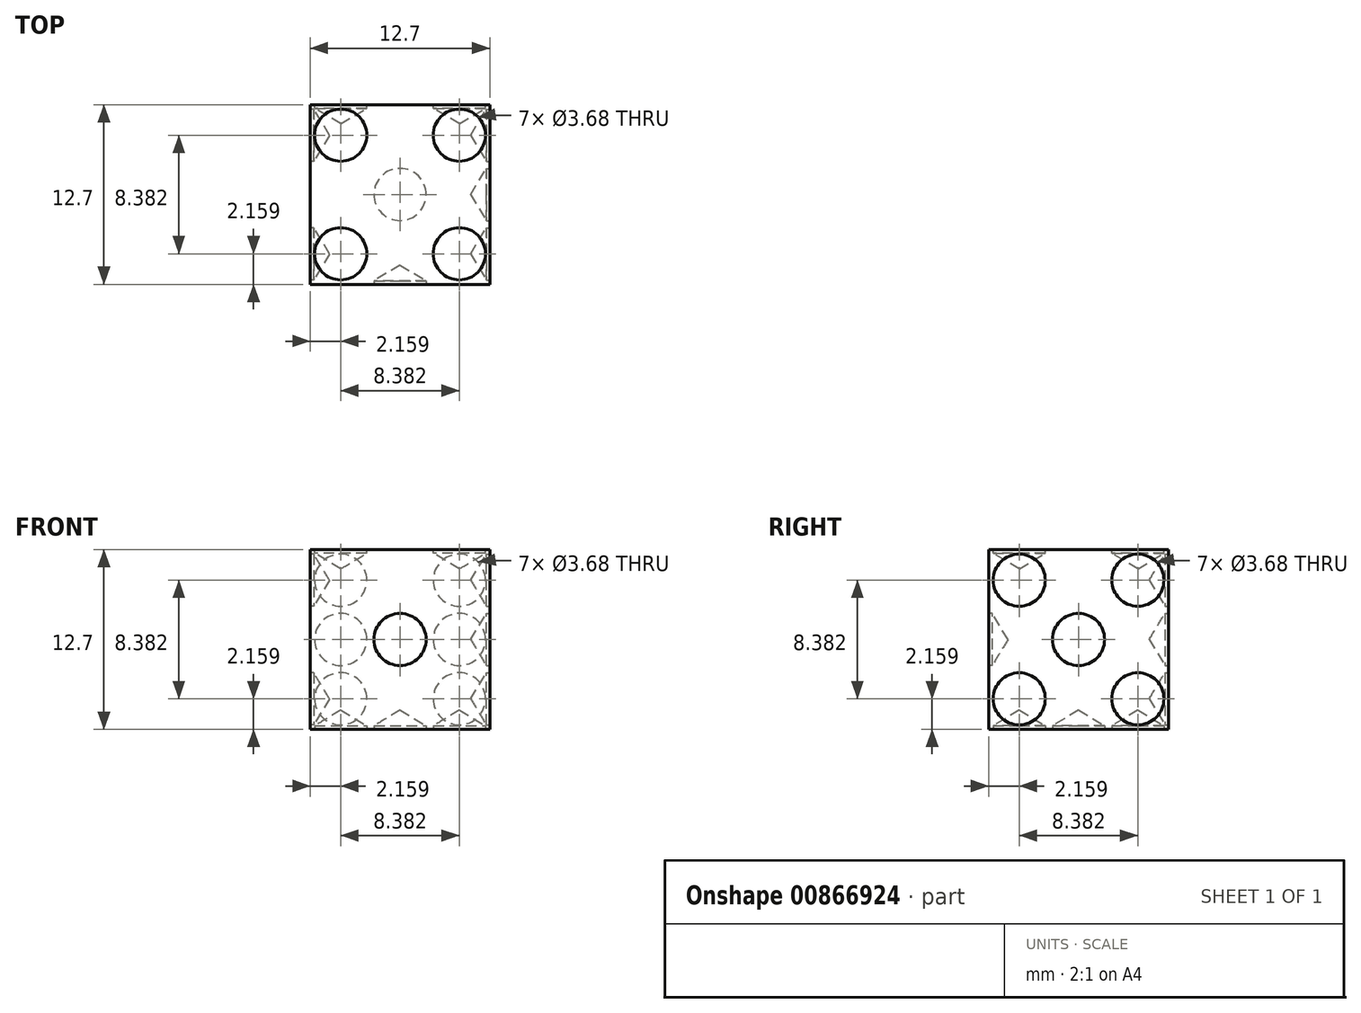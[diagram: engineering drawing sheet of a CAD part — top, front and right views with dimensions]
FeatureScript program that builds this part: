
annotation { "Feature Type Name" : "Feature", "Feature Type Description" : "" }
export const myFeature = defineFeature(function(context is Context, id is Id, definition is map)
    precondition{}
    {
        {
            var Q0;
            Q0=qCreatedBy(makeId("Top.planeOp"),FACE);
            var sketch = newSketch(context, id + "F0", { "sketchPlane" : qUnion([Q0])});
            skLineSegment(sketch, "E0.bottom", {"start": v(6.35, 6.35) * mm, "end": v(-6.35, 6.35) * mm});
            skLineSegment(sketch, "E0.top", {"start": v(6.35, -6.35) * mm, "end": v(-6.35, -6.35) * mm});
            skLineSegment(sketch, "E0.left", {"start": v(6.35, 6.35) * mm, "end": v(6.35, -6.35) * mm});
            skLineSegment(sketch, "E0.right", {"start": v(-6.35, 6.35) * mm, "end": v(-6.35, -6.35) * mm});
            skPoint(sketch, "E0.middle", {"position": v(0, 0) * mm});
            skSolve(sketch);
        }
        {
            var Q0;
            Q0=makeQuery(id+"F0.imprint","IMPRINT",FACE,{"disambiguationData":[TD([[makeQuery(id+"F0.imprint","IMPRINT",EDGE,{"derivedFrom":sQuery(id+"F0.wireOp",EDGE,"E0.bottom")}),1.0]])]});
            extrude(context, id + "F1", {"entities" : qUnion([Q0]), "depth" : 6.35 * mm, "offsetDistance" : 25.4 * mm, "hasSecondDirection" : true, "secondDirectionOppositeDirection" : true, "secondDirectionDepth" : 6.35 * mm});
        }
        {
            var Q0;
            Q0=makeQuery(id+"F1.opExtrude","CAP_FACE",FACE,{"disambiguationData":[OSD([sQuery(id+"F0.wireOp",EDGE,"E0.bottom"),sQuery(id+"F0.wireOp",EDGE,"E0.top"),sQuery(id+"F0.wireOp",EDGE,"E0.left"),sQuery(id+"F0.wireOp",EDGE,"E0.right")])],"isStart":false});
            var sketch = newSketch(context, id + "F2", { "sketchPlane" : qUnion([Q0])});
            skCircle(sketch, "E1", {"center": v(-4.2, 4.2) * mm, "radius": 1.9 * mm});
            skCircle(sketch, "E2", {"center": v(4.2, 4.2) * mm, "radius": 1.9 * mm});
            skCircle(sketch, "E3", {"center": v(-4.2, -4.2) * mm, "radius": 1.9 * mm});
            skCircle(sketch, "E4", {"center": v(4.2, -4.2) * mm, "radius": 1.9 * mm});
            skSolve(sketch);
        }
        {
            var Q0;
            Q0=makeQuery(id+"F1.opExtrude","SWEPT_FACE",FACE,{"disambiguationData":[OSD([sQuery(id+"F0.wireOp",EDGE,"E0.left")])]});
            var sketch = newSketch(context, id + "F3", { "sketchPlane" : qUnion([Q0])});
            skCircle(sketch, "E5", {"center": v(-4.2, 4.2) * mm, "radius": 1.9 * mm});
            skCircle(sketch, "E6", {"center": v(4.2, 4.2) * mm, "radius": 1.9 * mm});
            skCircle(sketch, "E7", {"center": v(0, 0) * mm, "radius": 1.9 * mm});
            skCircle(sketch, "E8", {"center": v(-4.2, -4.2) * mm, "radius": 1.9 * mm});
            skCircle(sketch, "E9", {"center": v(4.2, -4.2) * mm, "radius": 1.9 * mm});
            skSolve(sketch);
        }
        {
            var Q0;
            Q0=makeQuery(id+"F1.opExtrude","SWEPT_FACE",FACE,{"disambiguationData":[OSD([sQuery(id+"F0.wireOp",EDGE,"E0.top")])]});
            var sketch = newSketch(context, id + "F4", { "sketchPlane" : qUnion([Q0])});
            skCircle(sketch, "E10", {"center": v(0, 0) * mm, "radius": 1.9 * mm});
            skSolve(sketch);
        }
        {
            var Q0;
            Q0=makeQuery(id+"F1.opExtrude","CAP_FACE",FACE,{"disambiguationData":[OSD([sQuery(id+"F0.wireOp",EDGE,"E0.bottom"),sQuery(id+"F0.wireOp",EDGE,"E0.top"),sQuery(id+"F0.wireOp",EDGE,"E0.left"),sQuery(id+"F0.wireOp",EDGE,"E0.right")])],"isStart":true});
            var sketch = newSketch(context, id + "F5", { "sketchPlane" : qUnion([Q0])});
            skCircle(sketch, "E11", {"center": v(0, 0) * mm, "radius": 1.9 * mm});
            skCircle(sketch, "E12", {"center": v(-4.2, 4.2) * mm, "radius": 1.9 * mm});
            skCircle(sketch, "E13", {"center": v(4.2, -4.2) * mm, "radius": 1.9 * mm});
            skSolve(sketch);
        }
        {
            var Q0;
            Q0=makeQuery(id+"F1.opExtrude","SWEPT_FACE",FACE,{"disambiguationData":[OSD([sQuery(id+"F0.wireOp",EDGE,"E0.right")])]});
            var sketch = newSketch(context, id + "F6", { "sketchPlane" : qUnion([Q0])});
            skCircle(sketch, "E14", {"center": v(4.2, 4.2) * mm, "radius": 1.9 * mm});
            skCircle(sketch, "E15", {"center": v(-4.2, -4.2) * mm, "radius": 1.9 * mm});
            skSolve(sketch);
        }
        {
            var Q0;
            Q0=makeQuery(id+"F1.opExtrude","SWEPT_FACE",FACE,{"disambiguationData":[OSD([sQuery(id+"F0.wireOp",EDGE,"E0.bottom")])]});
            var sketch = newSketch(context, id + "F7", { "sketchPlane" : qUnion([Q0])});
            skCircle(sketch, "E16", {"center": v(-4.2, 4.2) * mm, "radius": 1.9 * mm});
            skCircle(sketch, "E17", {"center": v(-4.2, 0) * mm, "radius": 1.9 * mm});
            skCircle(sketch, "E18", {"center": v(-4.2, -4.2) * mm, "radius": 1.9 * mm});
            skCircle(sketch, "E19", {"center": v(4.2, -4.2) * mm, "radius": 1.9 * mm});
            skCircle(sketch, "E20", {"center": v(4.2, 0) * mm, "radius": 1.9 * mm});
            skCircle(sketch, "E21", {"center": v(4.2, 4.2) * mm, "radius": 1.9 * mm});
            skSolve(sketch);
        }
        {
            var Q0;
            Q0=sQuery(id+"F7.wireOp",VERTEX,"E16.center");
            var Q1;
            Q1=sQuery(id+"F7.wireOp",VERTEX,"E17.center");
            var Q2;
            Q2=sQuery(id+"F7.wireOp",VERTEX,"E18.center");
            var Q3;
            Q3=sQuery(id+"F7.wireOp",VERTEX,"E21.center");
            var Q4;
            Q4=sQuery(id+"F7.wireOp",VERTEX,"E20.center");
            var Q5;
            Q5=sQuery(id+"F7.wireOp",VERTEX,"E19.center");
            var Q6;
            Q6=makeQuery(id+"F1.opExtrude","SWEPT_BODY",BODY,{"disambiguationData":[OSD([sQuery(id+"F0.wireOp",EDGE,"E0.bottom"),sQuery(id+"F0.wireOp",EDGE,"E0.top"),sQuery(id+"F0.wireOp",EDGE,"E0.left"),sQuery(id+"F0.wireOp",EDGE,"E0.right")])]});
            hole(context, id + "F8", {"style" : HoleStyle.SIMPLE, "endStyle" : HoleEndStyle.BLIND, "holeDiameter" : 3.68 * mm, "majorDiameter" : 6.35 * mm, "holeDepth" : 0.25 * mm, "isTappedThrough" : true, "tappedDepth" : 12.7 * mm, "tapClearance" : 3, "locations" : qUnion([Q0, Q1, Q2, Q3, Q4, Q5]), "scope" : qUnion([Q6])});
        }
        {
            var Q0;
            Q0=sQuery(id+"F3.wireOp",VERTEX,"E5.center");
            var Q1;
            Q1=sQuery(id+"F3.wireOp",VERTEX,"E8.center");
            var Q2;
            Q2=sQuery(id+"F3.wireOp",VERTEX,"E6.center");
            var Q3;
            Q3=sQuery(id+"F3.wireOp",VERTEX,"E9.center");
            var Q4;
            Q4=sQuery(id+"F3.wireOp",VERTEX,"E7.center");
            var Q5;
            Q5=makeQuery(id+"F1.opExtrude","SWEPT_BODY",BODY,{"disambiguationData":[OSD([sQuery(id+"F0.wireOp",EDGE,"E0.bottom"),sQuery(id+"F0.wireOp",EDGE,"E0.top"),sQuery(id+"F0.wireOp",EDGE,"E0.left"),sQuery(id+"F0.wireOp",EDGE,"E0.right")])]});
            hole(context, id + "F9", {"style" : HoleStyle.SIMPLE, "endStyle" : HoleEndStyle.BLIND, "holeDiameter" : 3.68 * mm, "majorDiameter" : 6.35 * mm, "holeDepth" : 0.25 * mm, "isTappedThrough" : true, "tappedDepth" : 12.7 * mm, "tapClearance" : 3, "locations" : qUnion([Q0, Q1, Q2, Q3, Q4]), "scope" : qUnion([Q5])});
        }
        {
            var Q0;
            Q0=sQuery(id+"F6.wireOp",VERTEX,"E14.center");
            var Q1;
            Q1=sQuery(id+"F6.wireOp",VERTEX,"E15.center");
            var Q2;
            Q2=makeQuery(id+"F1.opExtrude","SWEPT_BODY",BODY,{"disambiguationData":[OSD([sQuery(id+"F0.wireOp",EDGE,"E0.bottom"),sQuery(id+"F0.wireOp",EDGE,"E0.top"),sQuery(id+"F0.wireOp",EDGE,"E0.left"),sQuery(id+"F0.wireOp",EDGE,"E0.right")])]});
            hole(context, id + "F10", {"style" : HoleStyle.SIMPLE, "endStyle" : HoleEndStyle.BLIND, "holeDiameter" : 3.68 * mm, "majorDiameter" : 6.35 * mm, "holeDepth" : 0.25 * mm, "isTappedThrough" : true, "tappedDepth" : 12.7 * mm, "tapClearance" : 3, "locations" : qUnion([Q0, Q1]), "scope" : qUnion([Q2])});
        }
        {
            var Q0;
            Q0=sQuery(id+"F2.wireOp",VERTEX,"E2.center");
            var Q1;
            Q1=sQuery(id+"F2.wireOp",VERTEX,"E4.center");
            var Q2;
            Q2=sQuery(id+"F2.wireOp",VERTEX,"E3.center");
            var Q3;
            Q3=sQuery(id+"F2.wireOp",VERTEX,"E1.center");
            var Q4;
            Q4=makeQuery(id+"F1.opExtrude","SWEPT_BODY",BODY,{"disambiguationData":[OSD([sQuery(id+"F0.wireOp",EDGE,"E0.bottom"),sQuery(id+"F0.wireOp",EDGE,"E0.top"),sQuery(id+"F0.wireOp",EDGE,"E0.left"),sQuery(id+"F0.wireOp",EDGE,"E0.right")])]});
            hole(context, id + "F11", {"style" : HoleStyle.SIMPLE, "endStyle" : HoleEndStyle.BLIND, "holeDiameter" : 3.68 * mm, "majorDiameter" : 6.35 * mm, "holeDepth" : 0.25 * mm, "isTappedThrough" : true, "tappedDepth" : 12.7 * mm, "tapClearance" : 3, "locations" : qUnion([Q0, Q1, Q2, Q3]), "scope" : qUnion([Q4])});
        }
        {
            var Q0;
            Q0=sQuery(id+"F5.wireOp",VERTEX,"E12.center");
            var Q1;
            Q1=sQuery(id+"F5.wireOp",VERTEX,"E11.center");
            var Q2;
            Q2=sQuery(id+"F5.wireOp",VERTEX,"E13.center");
            var Q3;
            Q3=makeQuery(id+"F1.opExtrude","SWEPT_BODY",BODY,{"disambiguationData":[OSD([sQuery(id+"F0.wireOp",EDGE,"E0.bottom"),sQuery(id+"F0.wireOp",EDGE,"E0.top"),sQuery(id+"F0.wireOp",EDGE,"E0.left"),sQuery(id+"F0.wireOp",EDGE,"E0.right")])]});
            hole(context, id + "F12", {"style" : HoleStyle.SIMPLE, "endStyle" : HoleEndStyle.BLIND, "holeDiameter" : 3.68 * mm, "majorDiameter" : 6.35 * mm, "holeDepth" : 0.25 * mm, "isTappedThrough" : true, "tappedDepth" : 12.7 * mm, "tapClearance" : 3, "locations" : qUnion([Q0, Q1, Q2]), "scope" : qUnion([Q3])});
        }
        {
            var Q0;
            Q0=sQuery(id+"F4.wireOp",VERTEX,"E10.center");
            var Q1;
            Q1=makeQuery(id+"F1.opExtrude","SWEPT_BODY",BODY,{"disambiguationData":[OSD([sQuery(id+"F0.wireOp",EDGE,"E0.bottom"),sQuery(id+"F0.wireOp",EDGE,"E0.top"),sQuery(id+"F0.wireOp",EDGE,"E0.left"),sQuery(id+"F0.wireOp",EDGE,"E0.right")])]});
            hole(context, id + "F13", {"style" : HoleStyle.SIMPLE, "endStyle" : HoleEndStyle.BLIND, "holeDiameter" : 3.68 * mm, "majorDiameter" : 6.35 * mm, "holeDepth" : 0.25 * mm, "isTappedThrough" : true, "tappedDepth" : 12.7 * mm, "tapClearance" : 3, "locations" : qUnion([Q0]), "scope" : qUnion([Q1])});
        }
    });
